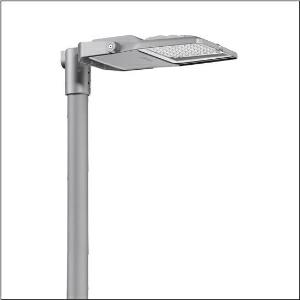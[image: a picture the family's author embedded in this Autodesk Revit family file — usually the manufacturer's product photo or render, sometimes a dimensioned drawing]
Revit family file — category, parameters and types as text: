
# Revit family: floodlight_fl_21_mini___pl52_5xa7775d2d3a_ca02
name_source: partatom
category: Lighting Fixtures
units: mm (PartAtom-declared; Revit-internal decimal feet)

## family parameters
Cut with Voids When Loaded = No
Host = Face
Light Source = No
Part Type = Normal
Room Calculation Point = No
Round Connector Dimension = Use Diameter
Shared = No

## types (1)
- --- (1 x LED, 17840 lm, 142.9 W, 3000K)
    Apparent Load = 143 VA
    CIE Flux Codes = 26 60 98 100 100
    Color Rendering = 70
    Color Temperature = 3000K
    Default Elevation = 1800 mm
    Description = Floodlight FL 21 mini, floodlight, primary light control with lens, of PMMA, primary optical cover: protective disc, of toughened safety glass, transparent, light distribution: PL52, light emission: direct distribution, installation type: surface-mounted, LED, High Power LED, rated luminous flux: 17.840lm, luminous efficacy: 125lm/W, light colour: 730, colour temperature: 3000K, control: flexible luminous flux parameterisation, time-dependent luminous flux control, constant luminous flux control, overheat protection, presetting dimming logarithmic, with terminal, 6-pole, mains connection: 220..240V, AC, 50/60Hz, start of lifetime: 143W, end of service life: 151W, reduction: 63W, luminaire housing, of diecast aluminium, powder-coated, Siteco® metallic grey (DB 702S), corrosivity category C5 mid according to DIN EN ISO 12944, sealing non-destructively replaceable, please order mast flange separately, mast bracket, of steel, galvanised, powder-coated, Siteco® metallic grey (DB 702S), Smart Interface above, protection rating (complete): IP66, insulation class (complete): insulation class II (safety insulation), certification: CE, ENEC, VDE, protection symbol: D, impact resistance: IK08, permissible operating ambient temperature: -40..+40°C, permissible operating ambient temperature for outdoor applications: -40..+50°C, standard: DIN EN 12944, LABS conformity tested according to VDMA 24364:2018-05, packaging unit: 1 piece

Light Distribution: PL52
    Height = 70 mm
    Lamp = 1 x LED
    Lamp Light Flux = 17840 lm
    Lamp Power = 142.9 W
    Lamp count = 1
    Length = 485 mm
    Luminous efficacy = 125 lm/W
    Manufacturer = Siteco
    ModVariant = No
    Model = 5XA7775D2D3A
    Number of Poles = 1
    OnlyDefault = Yes
    Power Factor = 1
    Product Name = Floodlight FL 21 mini | PL52
    Product group = floodlight | pylon annexe
    ProductGroupID = 6200
    Protection Class = Protection class II
    Protection Degree = IP 66
    RLX_Detail_Level = 1
    RLX_Emergency_Light_Flux = 0 lm
    RLX_Emergency_Type = 0
    RLX_Emergency_Type_DB = No
    RlxData = <blob elided: 101441 chars, md5=43bf2460>
    Socket = socket
    Standby Power = 0 W
    System Light Flux = 17840 lm
    System Power = 143 W
    Type Comments = factory setting: luminous flux: 100 % | dim-lin: 254 | 730 mA
    Type Image = l_1007125.jpg
    URL = http://relux.com
    VarID = @adj_095485
    Voltage = 0 V
    Weight = 0.00 kg
    Width = 337 mm

## geometry (parser evidence)
native form markers: Blend x4, Sweep x13
no freeform markers — native parametric forms only
